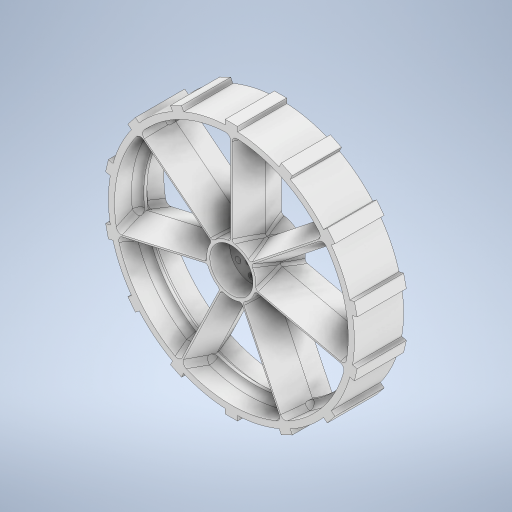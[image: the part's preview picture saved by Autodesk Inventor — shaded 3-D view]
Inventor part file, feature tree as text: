
AUTODESK INVENTOR PART (.ipt)
format: ipt  version: 2023 (Build 270158000, 158)  size: 1,280,512 bytes
history: native  units: in
note: dims shown in document units (in); Inventor stores cm internally (conversion verified against a paired STEP export)
features: extrude x6, sketch x6, pattern_circular x5, projected_geometry x5, fillet x3, mirror x2, plane x1
ambient origin geometry x8: Origin, YZ Plane, XZ Plane, XY Plane, X Axis, Y Axis, Z Axis, Center Point
bodies: Solid1 (feature_tree)
feature tree (28):
  extrude  "Extrusion1"  Depth=0.25in
  extrude  "Extrusion2"  TaperAngle=0.0deg  [1 undecoded]
  extrude  "Extrusion3"  Depth=0.5787in
  extrude  "Extrusion4"  Depth=0.625in
  pattern_circular  "Circular Pattern1"  Count=6 Angle=360.0deg
  extrude  "Extrusion5"  TaperAngle=0.0deg  [1 undecoded]
  plane  "Work Plane1"
  extrude  "Extrusion6"  Depth=0.0787in
  pattern_circular  "Circular Pattern2"  [2 undecoded]
  fillet  "Fillet1"  [1 undecoded]
  mirror  "Mirror1"
  pattern_circular  "Circular Pattern3"  Count=2  [1 undecoded]
  fillet  "Fillet2"  Radius=0.0787in
  mirror  "Mirror2"
  pattern_circular  "Circular Pattern4"  [2 undecoded]
  fillet  "Fillet4"  Radius=0.0787in
  pattern_circular  "Circular Pattern6"  [2 undecoded]
  sketch  "Sketch1"  dims[d0=10.0in d2=0.25in]
  sketch  "Sketch2"  dims[d3=2.0in d4=0.0in]
  sketch  "Sketch3"  dims[d5=2.0in d7=0.5787in]
  sketch  "Sketch4"  dims[d8=0.2362in d9=0.625in d10=2.3622in d12=360.0deg]
  sketch  "Sketch5"  dims[d14=0.375in d15=0.0in]
  sketch  "Sketch6"  dims[d16=2.0in d17=0.125in d18=2.0in d19=0.0in d21=0.7874in d22=0.0787in d23=0.0787in d24=0.0787in d25=0.063in d26=2.0in d27=0.0in d28=2.7559in d29=360.0deg d32=0.125in d33=0.0in d34=2.0in d35=0.5in d36=4.9375in d37=0.25in d38=0.0in d39=5.5118in d40=360.0deg d42=0.25in d43=2.7559in d44=360.0deg d46=0.1969in d47=2.7559in d48=360.0deg d54=0.1181in d55=2.7559in d56=360.0deg]
  projected_geometry  "Project Cut Edges1"
  projected_geometry  "Project Cut Edges2"
  projected_geometry  "Project Cut Edges3"
  projected_geometry  "Project Cut Edges4"
  projected_geometry  "Project Cut Edges5"
note: 10 required parameter values undecoded (feature->parameter linkage not recoverable at this tier; creation-order binding heuristic only, values carry confidence <= 0.55)
